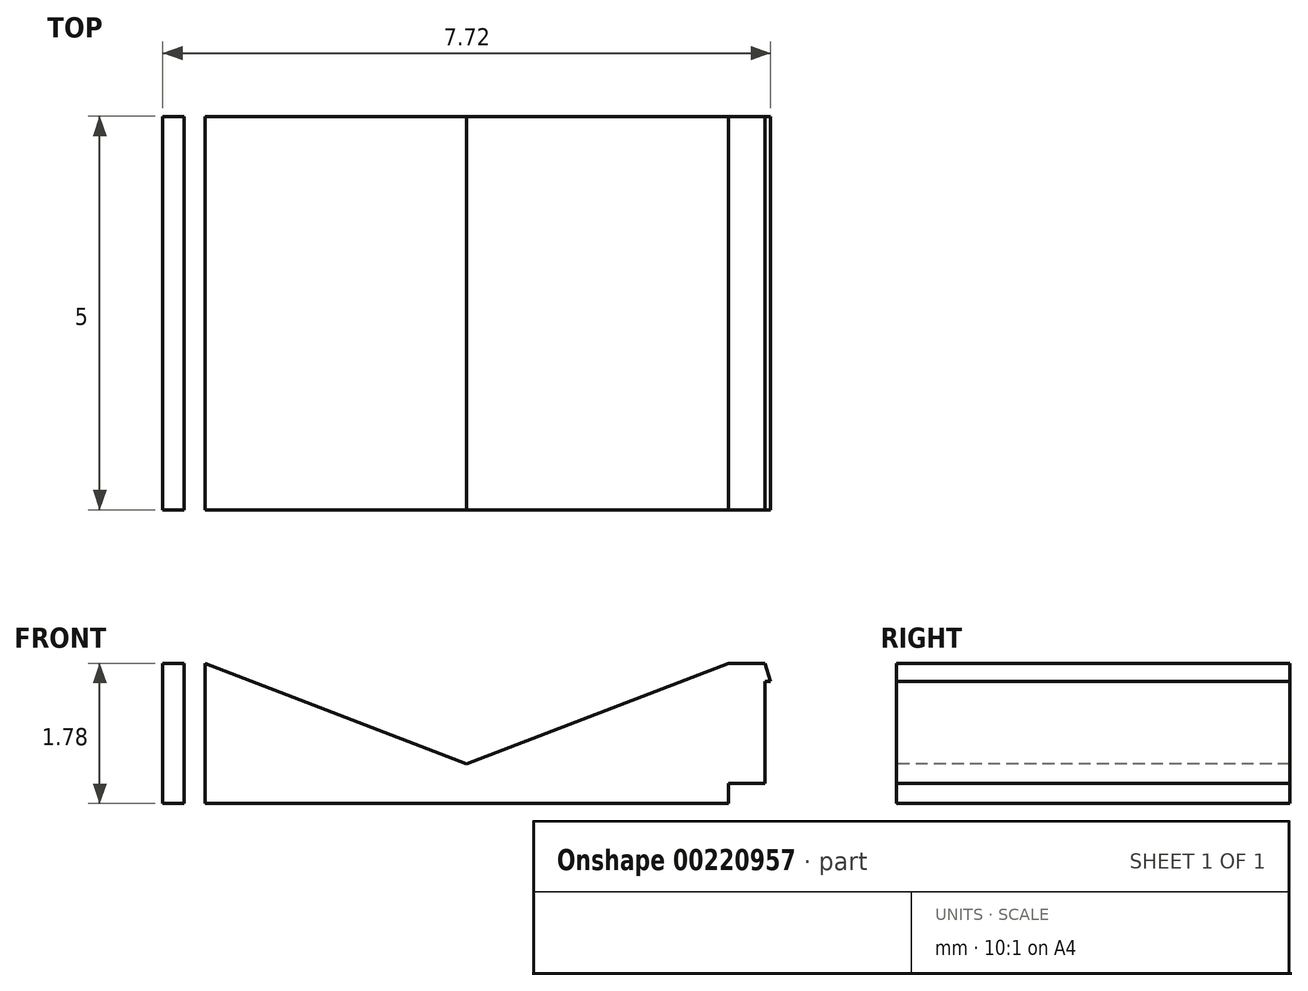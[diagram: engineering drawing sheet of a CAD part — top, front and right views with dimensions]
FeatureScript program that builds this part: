
annotation { "Feature Type Name" : "Feature", "Feature Type Description" : "" }
export const myFeature = defineFeature(function(context is Context, id is Id, definition is map)
    precondition{}
    {
        {
            var Q0;
            Q0=qCreatedBy(makeId("Top.planeOp"),FACE);
            var sketch = newSketch(context, id + "F0", { "sketchPlane" : qUnion([Q0])});
            skLineSegment(sketch, "E0.bottom", {"start": v(3.32, 2.68) * mm, "end": v(-3.32, 2.68) * mm});
            skLineSegment(sketch, "E0.top", {"start": v(3.32, -2.32) * mm, "end": v(-3.32, -2.32) * mm});
            skLineSegment(sketch, "E0.left", {"start": v(3.32, 2.68) * mm, "end": v(3.32, -2.32) * mm});
            skLineSegment(sketch, "E0.right", {"start": v(-3.32, 2.68) * mm, "end": v(-3.32, -2.32) * mm});
            skPoint(sketch, "E0.middle", {"position": v(0, 0.18) * mm});
            skSolve(sketch);
        }
        {
            var Q0;
            Q0 = qSketchRegion(id + "F0", true);
            extrude(context, id + "F1", {"entities" : qUnion([Q0]), "depth" : 1.78 * mm});
        }
        {
            var Q0;
            Q0=makeQuery(id+"F1.opExtrude","SWEPT_FACE",FACE,{"disambiguationData":[OSD([sQuery(id+"F0.wireOp",EDGE,"E0.top")])]});
            var sketch = newSketch(context, id + "F2", { "sketchPlane" : qUnion([Q0])});
            skLineSegment(sketch, "E1", {"start": v(0, 0.5) * mm, "end": v(3.32, 1.78) * mm});
            skLineSegment(sketch, "E2", {"start": v(-3.32, 1.78) * mm, "end": v(0, 0.5) * mm});
            skSolve(sketch);
        }
        {
            var Q0;
            Q0 = qSketchRegion(id + "F2", true);
            var Q1;
            Q1=makeQuery(id+"F2.imprint","IMPRINT",FACE,{"disambiguationData":[TD([[makeQuery(id+"F2.imprint","IMPRINT",EDGE,{"derivedFrom":sQuery(id+"F2.wireOp",EDGE,"E1")}),1.0]])]});
            extrude(context, id + "F3", {"entities" : qUnion([Q0, Q1]), "operationType" : NewBodyOperationType.REMOVE, "oppositeDirection" : true, "depth" : 25.4 * mm});
        }
        {
            var Q0;
            Q0=makeQuery(id+"F1.opExtrude","SWEPT_FACE",FACE,{"disambiguationData":[OSD([sQuery(id+"F0.wireOp",EDGE,"E0.top")])]});
            var sketch = newSketch(context, id + "F4", { "sketchPlane" : qUnion([Q0])});
            skLineSegment(sketch, "E3.bottom", {"start": v(3.32, 1.78) * mm, "end": v(3.86, 1.78) * mm});
            skLineSegment(sketch, "E3.top", {"start": v(3.32, 0) * mm, "end": v(3.86, 0) * mm});
            skLineSegment(sketch, "E3.left", {"start": v(3.32, 1.78) * mm, "end": v(3.32, 0) * mm});
            skLineSegment(sketch, "E3.right", {"start": v(3.86, 1.78) * mm, "end": v(3.86, 0) * mm});
            skLineSegment(sketch, "E4.bottom", {"start": v(-3.32, 0) * mm, "end": v(-3.86, 0) * mm});
            skLineSegment(sketch, "E4.top", {"start": v(-3.32, 1.78) * mm, "end": v(-3.86, 1.78) * mm});
            skLineSegment(sketch, "E4.left", {"start": v(-3.32, 0) * mm, "end": v(-3.32, 1.78) * mm});
            skLineSegment(sketch, "E4.right", {"start": v(-3.86, 0) * mm, "end": v(-3.86, 1.78) * mm});
            skLineSegment(sketch, "E5.top", {"start": v(-3.32, 0) * mm, "end": v(-3.6, 0) * mm});
            skLineSegment(sketch, "E5.left", {"start": v(-3.32, 1.78) * mm, "end": v(-3.32, 0) * mm});
            skLineSegment(sketch, "E5.right", {"start": v(-3.6, 1.78) * mm, "end": v(-3.6, 0) * mm});
            skLineSegment(sketch, "E6.top", {"start": v(-3.32, 0.26) * mm, "end": v(-3.86, 0.26) * mm});
            skLineSegment(sketch, "E6.left", {"start": v(-3.32, 0) * mm, "end": v(-3.32, 0.26) * mm});
            skLineSegment(sketch, "E6.right", {"start": v(-3.86, 0) * mm, "end": v(-3.86, 0.26) * mm});
            skLineSegment(sketch, "E7.bottom", {"start": v(3.32, 1.78) * mm, "end": v(3.6, 1.78) * mm});
            skLineSegment(sketch, "E7.top", {"start": v(3.32, 0) * mm, "end": v(3.6, 0) * mm});
            skLineSegment(sketch, "E7.right", {"start": v(3.6, 1.78) * mm, "end": v(3.6, 0) * mm});
            skLineSegment(sketch, "E8.top", {"start": v(3.32, 0.26) * mm, "end": v(3.86, 0.26) * mm});
            skLineSegment(sketch, "E8.left", {"start": v(3.32, 0) * mm, "end": v(3.32, 0.26) * mm});
            skLineSegment(sketch, "E8.right", {"start": v(3.86, 0) * mm, "end": v(3.86, 0.26) * mm});
            skSolve(sketch);
        }
        {
            var Q0;
            {var subQ0=sQuery(id+"F4.wireOp",EDGE,"E4.right");Q0=makeQuery(id+"F4.imprint","IMPRINT",FACE,{"disambiguationData":[TD([[makeQuery(id+"F4.imprint","IMPRINT",EDGE,{"derivedFrom":subQ0}),-1.0]])]});}
            var Q1;
            {var subQ5=sQuery(id+"F4.wireOp",EDGE,"E6.right");Q1=makeQuery(id+"F4.imprint","IMPRINT",FACE,{"disambiguationData":[TD([[makeQuery(id+"F4.imprint","IMPRINT",EDGE,{"derivedFrom":subQ5}),-1.0]])]});}
            var Q2;
            {var subQ5=sQuery(id+"F4.wireOp",EDGE,"E6.left");Q2=makeQuery(id+"F4.imprint","IMPRINT",FACE,{"disambiguationData":[TD([[makeQuery(id+"F4.imprint","IMPRINT",EDGE,{"derivedFrom":subQ5}),-1.0]])]});}
            var Q3;
            {var subQ5=sQuery(id+"F4.wireOp",EDGE,"E8.left");Q3=makeQuery(id+"F4.imprint","IMPRINT",FACE,{"disambiguationData":[TD([[makeQuery(id+"F4.imprint","IMPRINT",EDGE,{"derivedFrom":subQ5}),1.0]])]});}
            var Q4;
            {var subQ5=sQuery(id+"F4.wireOp",EDGE,"E8.right");Q4=makeQuery(id+"F4.imprint","IMPRINT",FACE,{"disambiguationData":[TD([[makeQuery(id+"F4.imprint","IMPRINT",EDGE,{"derivedFrom":subQ5}),1.0]])]});}
            var Q5;
            {var subQ0=sQuery(id+"F4.wireOp",EDGE,"E3.bottom");Q5=makeQuery(id+"F4.imprint","IMPRINT",FACE,{"disambiguationData":[TD([[makeQuery(id+"F4.imprint","IMPRINT",EDGE,{"derivedFrom":subQ0}),-1.0]])]});}
            var Q6;
            Q6=makeQuery(id+"F1.opExtrude","SWEPT_FACE",FACE,{"disambiguationData":[OSD([sQuery(id+"F0.wireOp",EDGE,"E0.bottom")])]});
            extrude(context, id + "F5", {"entities" : qUnion([Q0, Q1, Q2, Q3, Q4, Q5]), "operationType" : NewBodyOperationType.ADD, "endBound" : BoundingType.UP_TO_SURFACE, "oppositeDirection" : true, "endBoundEntityFace" : qUnion([Q6]), "depth" : 25.4 * mm});
        }
        {
            var Q0;
            {var subQ0=sQuery(id+"F0.wireOp",EDGE,"E0.bottom");Q0=makeQuery(id+"F5.boolean.opBoolean","MERGE",FACE,{"derivedFrom":[makeQuery(id+"F1.opExtrude","SWEPT_FACE",FACE,{"disambiguationData":[OSD([subQ0])]}),makeQuery(id+"F5.opExtrude","CAP_FACE",FACE,{"disambiguationData":[OSD([subQ0]),ownerDisambiguation([makeQuery(id+"F5.opExtrude","SWEPT_BODY",BODY,{"disambiguationData":[OSD([sQuery(id+"F4.wireOp",EDGE,"E3.bottom"),sQuery(id+"F4.wireOp",EDGE,"E3.right"),sQuery(id+"F4.wireOp",EDGE,"E7.right"),sQuery(id+"F4.wireOp",EDGE,"E3.top"),sQuery(id+"F4.wireOp",EDGE,"E8.top"),sQuery(id+"F4.wireOp",EDGE,"E8.left"),sQuery(id+"F4.wireOp",EDGE,"E8.right")])]})])],"isStart":false}),makeQuery(id+"F5.opExtrude","CAP_FACE",FACE,{"disambiguationData":[OSD([subQ0]),ownerDisambiguation([makeQuery(id+"F5.opExtrude","SWEPT_BODY",BODY,{"disambiguationData":[OSD([sQuery(id+"F4.wireOp",EDGE,"E4.top"),sQuery(id+"F4.wireOp",EDGE,"E4.right"),sQuery(id+"F4.wireOp",EDGE,"E5.right"),sQuery(id+"F4.wireOp",EDGE,"E4.bottom"),sQuery(id+"F4.wireOp",EDGE,"E6.top"),sQuery(id+"F4.wireOp",EDGE,"E6.left"),sQuery(id+"F4.wireOp",EDGE,"E6.right")])]})])],"isStart":false})]});}
            var sketch = newSketch(context, id + "F6", { "sketchPlane" : qUnion([Q0])});
            skLineSegment(sketch, "E9", {"start": v(-3.86, 1.55) * mm, "end": v(-3.79, 1.55) * mm});
            skLineSegment(sketch, "E10", {"start": v(-3.86, 1.55) * mm, "end": v(-3.79, 1.78) * mm});
            skLineSegment(sketch, "E11", {"start": v(-3.79, 1.78) * mm, "end": v(-3.79, 1.55) * mm});
            skLineSegment(sketch, "E12", {"start": v(-3.79, 1.55) * mm, "end": v(-3.79, 0) * mm});
            skLineSegment(sketch, "E13", {"start": v(3.86, 1.55) * mm, "end": v(3.78, 1.55) * mm});
            skLineSegment(sketch, "E14", {"start": v(3.86, 1.55) * mm, "end": v(3.78, 1.78) * mm});
            skLineSegment(sketch, "E15", {"start": v(3.78, 1.78) * mm, "end": v(3.78, 1.55) * mm});
            skLineSegment(sketch, "E16", {"start": v(3.78, 1.55) * mm, "end": v(3.78, 0) * mm});
            skSolve(sketch);
        }
        {
            var Q0;
            {var subQ0=sQuery(id+"F6.wireOp",EDGE,"E9");Q0=makeQuery(id+"F6.imprint","IMPRINT",FACE,{"disambiguationData":[TD([[makeQuery(id+"F6.imprint","IMPRINT",EDGE,{"derivedFrom":subQ0}),-1.0]])]});}
            var Q1;
            {var subQ0=sQuery(id+"F6.wireOp",EDGE,"E10");Q1=makeQuery(id+"F6.imprint","IMPRINT",FACE,{"disambiguationData":[TD([[makeQuery(id+"F6.imprint","IMPRINT",EDGE,{"derivedFrom":subQ0}),1.0]])]});}
            var Q2;
            {var subQ0=sQuery(id+"F6.wireOp",EDGE,"E14");Q2=makeQuery(id+"F6.imprint","IMPRINT",FACE,{"disambiguationData":[TD([[makeQuery(id+"F6.imprint","IMPRINT",EDGE,{"derivedFrom":subQ0}),-1.0]])]});}
            var Q3;
            {var subQ0=sQuery(id+"F6.wireOp",EDGE,"E13");Q3=makeQuery(id+"F6.imprint","IMPRINT",FACE,{"disambiguationData":[TD([[makeQuery(id+"F6.imprint","IMPRINT",EDGE,{"derivedFrom":subQ0}),1.0]])]});}
            extrude(context, id + "F7", {"entities" : qUnion([Q0, Q1, Q2, Q3]), "operationType" : NewBodyOperationType.REMOVE, "oppositeDirection" : true, "depth" : 25.4 * mm});
        }
    });
